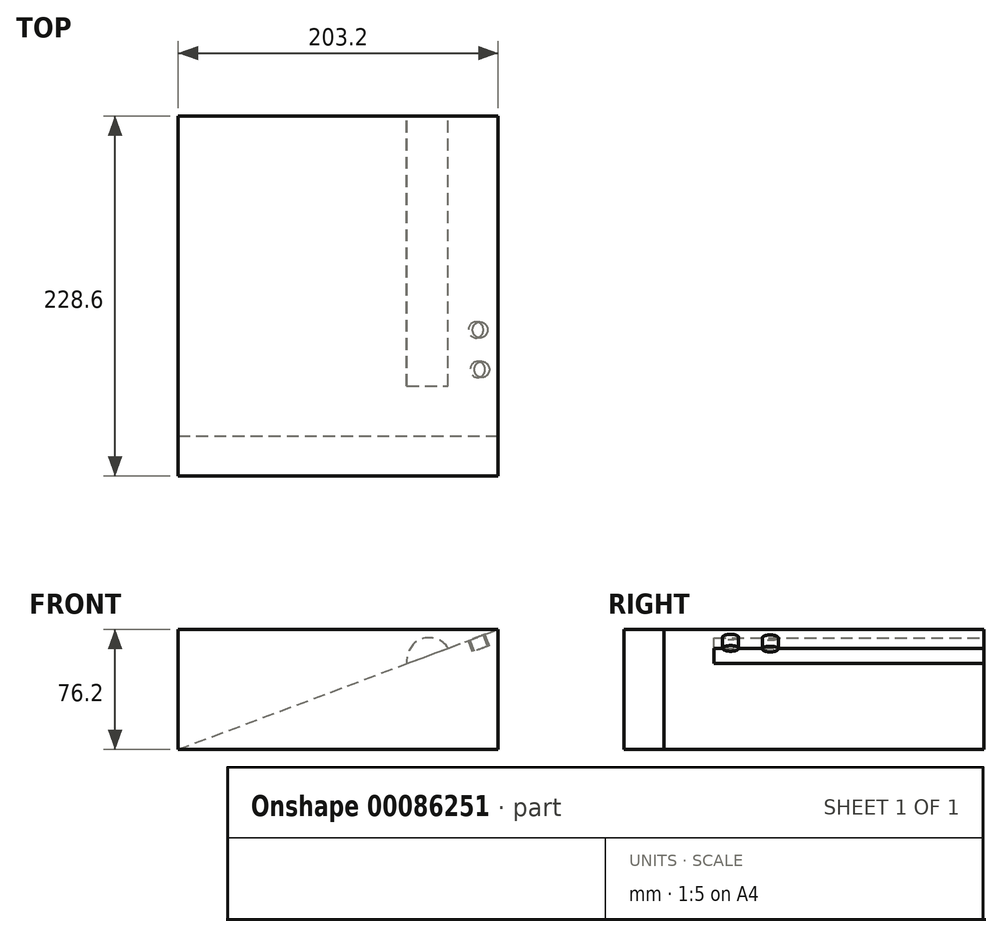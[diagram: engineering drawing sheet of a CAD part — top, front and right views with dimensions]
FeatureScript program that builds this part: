
annotation { "Feature Type Name" : "Feature", "Feature Type Description" : "" }
export const myFeature = defineFeature(function(context is Context, id is Id, definition is map)
    precondition{}
    {
        {
            var Q0;
            Q0=qCreatedBy(makeId("Top.planeOp"),FACE);
            var sketch = newSketch(context, id + "F0", { "sketchPlane" : qUnion([Q0])});
            skLineSegment(sketch, "E0.bottom", {"start": v(-75.3, 151.48) * mm, "end": v(127.9, 151.48) * mm});
            skLineSegment(sketch, "E0.top", {"start": v(-75.3, -77.12) * mm, "end": v(127.9, -77.12) * mm});
            skLineSegment(sketch, "E0.left", {"start": v(-75.3, 151.48) * mm, "end": v(-75.3, -77.12) * mm});
            skLineSegment(sketch, "E0.right", {"start": v(127.9, 151.48) * mm, "end": v(127.9, -77.12) * mm});
            skSolve(sketch);
        }
        {
            var Q0;
            Q0=makeQuery(id+"F0.imprint","IMPRINT",FACE,{"disambiguationData":[TD([[makeQuery(id+"F0.imprint","IMPRINT",EDGE,{"derivedFrom":sQuery(id+"F0.wireOp",EDGE,"E0.bottom")}),-1.0]])]});
            extrude(context, id + "F1", {"entities" : qUnion([Q0]), "depth" : 76.2 * mm});
        }
        {
            var Q0;
            Q0=makeQuery(id+"F1.opExtrude","SWEPT_FACE",FACE,{"disambiguationData":[OSD([sQuery(id+"F0.wireOp",EDGE,"E0.bottom")])]});
            var sketch = newSketch(context, id + "F2", { "sketchPlane" : qUnion([Q0])});
            skLineSegment(sketch, "E1", {"start": v(75.3, 0) * mm, "end": v(-127.9, 76.2) * mm});
            skSolve(sketch);
        }
        {
            var Q0;
            Q0=makeQuery(id+"F2.imprint","IMPRINT",FACE,{"disambiguationData":[TD([[makeQuery(id+"F2.imprint","IMPRINT",EDGE,{"derivedFrom":sQuery(id+"F2.wireOp",EDGE,"E1")}),1.0]])]});
            extrude(context, id + "F3", {"entities" : qUnion([Q0]), "operationType" : NewBodyOperationType.REMOVE, "oppositeDirection" : true, "depth" : 203.2 * mm});
        }
        {
            var Q0;
            Q0=makeQuery(id+"F1.opExtrude","SWEPT_FACE",FACE,{"disambiguationData":[OSD([sQuery(id+"F0.wireOp",EDGE,"E0.bottom")])]});
            var sketch = newSketch(context, id + "F4", { "sketchPlane" : qUnion([Q0])});
            skArc(sketch, "E2", {"start": v(-70, 54.5) * mm, "mid": v(-79.12, 70) * mm, "end": v(-96.17, 64.3) * mm});
            skLineSegment(sketch, "E3", {"start": v(-70, 54.5) * mm, "end": v(-96.17, 64.3) * mm});
            skSolve(sketch);
        }
        {
            var Q0;
            Q0=makeQuery(id+"F4.imprint","IMPRINT",FACE,{"disambiguationData":[TD([[makeQuery(id+"F4.imprint","IMPRINT",EDGE,{"derivedFrom":sQuery(id+"F4.wireOp",EDGE,"E2")}),1.0]])]});
            extrude(context, id + "F5", {"entities" : qUnion([Q0]), "operationType" : NewBodyOperationType.REMOVE, "oppositeDirection" : true, "depth" : 171.45 * mm});
        }
        {
            var Q0;
            Q0=makeQuery(id+"F5.boolean.opBoolean","SPLIT",FACE,{"disambiguationData":[TD([makeQuery(id+"F1.opExtrude","SWEPT_FACE",FACE,{"disambiguationData":[OSD([sQuery(id+"F0.wireOp",EDGE,"E0.left")])]})])],"derivedFrom":makeQuery(id+"F3.boolean.opBoolean","COPY",FACE,{"derivedFrom":makeQuery(id+"F3.opExtrude","SWEPT_FACE",FACE,{"disambiguationData":[OSD([sQuery(id+"F2.wireOp",EDGE,"E1")])]})})});
            var sketch = newSketch(context, id + "F6", { "sketchPlane" : qUnion([Q0])});
            skCircle(sketch, "E4", {"center": v(131.44, -15.68) * mm, "radius": 5.08 * mm});
            skCircle(sketch, "E5", {"center": v(132.6, 9.47) * mm, "radius": 5.08 * mm});
            skSolve(sketch);
        }
        {
            var Q0;
            Q0=makeQuery(id+"F6.imprint","IMPRINT",FACE,{"disambiguationData":[TD([[makeQuery(id+"F6.imprint","IMPRINT",EDGE,{"derivedFrom":sQuery(id+"F6.wireOp",EDGE,"E4")}),1.0]])]});
            var Q1;
            Q1 = qSketchRegion(id + "F6", true);
            var Q2;
            Q2=makeQuery(id+"F6.imprint","IMPRINT",FACE,{"disambiguationData":[TD([[makeQuery(id+"F6.imprint","IMPRINT",EDGE,{"derivedFrom":sQuery(id+"F6.wireOp",EDGE,"E5")}),1.0]])]});
            extrude(context, id + "F7", {"entities" : qUnion([Q0, Q1, Q2]), "operationType" : NewBodyOperationType.ADD, "depth" : 7.62 * mm});
        }
        {
            var Q0;
            Q0=makeQuery(id+"F5.boolean.opBoolean","COPY",FACE,{"derivedFrom":makeQuery(id+"F5.opExtrude","CAP_FACE",FACE,{"disambiguationData":[OSD([sQuery(id+"F4.wireOp",EDGE,"E2"),sQuery(id+"F4.wireOp",EDGE,"E3")])],"isStart":false})});
            cPlane(context, id + "F8", {"entities" : qUnion([Q0]), "cplaneType" : CPlaneType.OFFSET, "offset" : 152.4 * mm, "width" : 152.4 * mm, "height" : 152.4 * mm});
        }
    });
